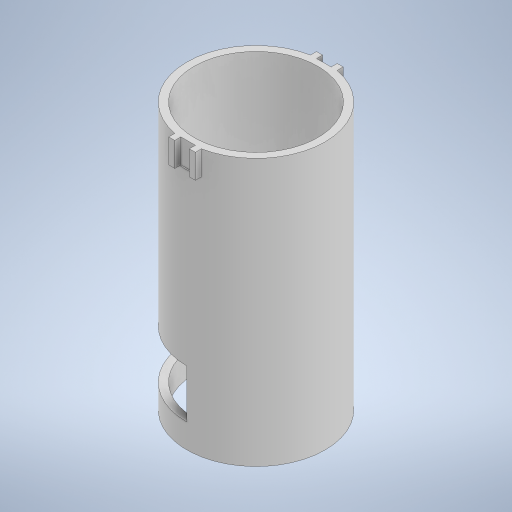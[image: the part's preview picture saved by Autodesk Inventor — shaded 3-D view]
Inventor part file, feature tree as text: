
AUTODESK INVENTOR PART (.ipt)
format: ipt  version: 2024.3 (Build 283343000, 343)  size: 274,944 bytes
history: native  units: mm
features: extrude x4, sketch x4, mirror x2, plane x1
ambient origin geometry x8: Origin, YZ Plane, XZ Plane, XY Plane, X Axis, Y Axis, Z Axis, Center Point
bodies: Solid1 (feature_tree)
feature tree (11):
  extrude  "Extrusion1"  Depth=102.0mm
  extrude  "Extrusion2"  Depth=20.0mm TaperAngle=0.0deg
  plane  "Work Plane1"
  extrude  "Extrusion3"  Depth=5.0mm
  mirror  "Mirror1"
  mirror  "Mirror2"
  sketch  "Sketch4"  dims[d8=5.0mm d9=20.0mm d10=0.0mm d11=40.0mm d12=36.0mm d13=2.0mm d14=20.0mm d15=0.0mm d16=0.0mm d19=21.99994mm]
  extrude  "Extrusion4"  Depth=20.0mm TaperAngle=0.0deg
  sketch  "Sketch1"  dims[d0=114.0mm d1=102.0mm]
  sketch  "Sketch2"  dims[d2=220.0mm d3=0.0mm d4=20.0mm d5=0.0mm]
  sketch  "Sketch3"  dims[d6=0.0mm d7=5.0mm]
